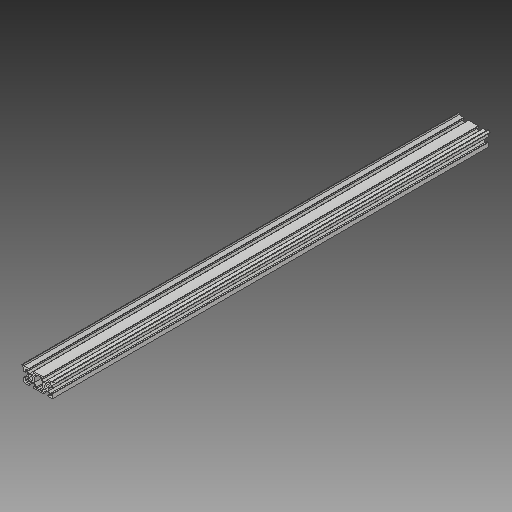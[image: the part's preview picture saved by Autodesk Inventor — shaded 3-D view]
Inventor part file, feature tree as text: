
AUTODESK INVENTOR PART (.ipt)
format: ipt  version: 2017 (Build 210142000, 142)  size: 232,960 bytes
history: native  units: mm
features: other x2, extrude x1, sketch x1, reference x1
ambient origin geometry x8: Origin, YZ Plane, XZ Plane, XY Plane, X Axis, Y Axis, Z Axis, Center Point
bodies: Solid1 (feature_tree)
feature tree (5):
  extrude  "Extrusion1"  [1 undecoded]
  sketch  "Sketch1"  dims[d0=600.0mm d1=0.0mm]
  reference  "Reference1"
  other  "Assembly3"
  other  "Makerslide Default 300mm:1"
note: 1 required parameter value undecoded (feature->parameter linkage not recoverable at this tier; creation-order binding heuristic only, values carry confidence <= 0.55)
